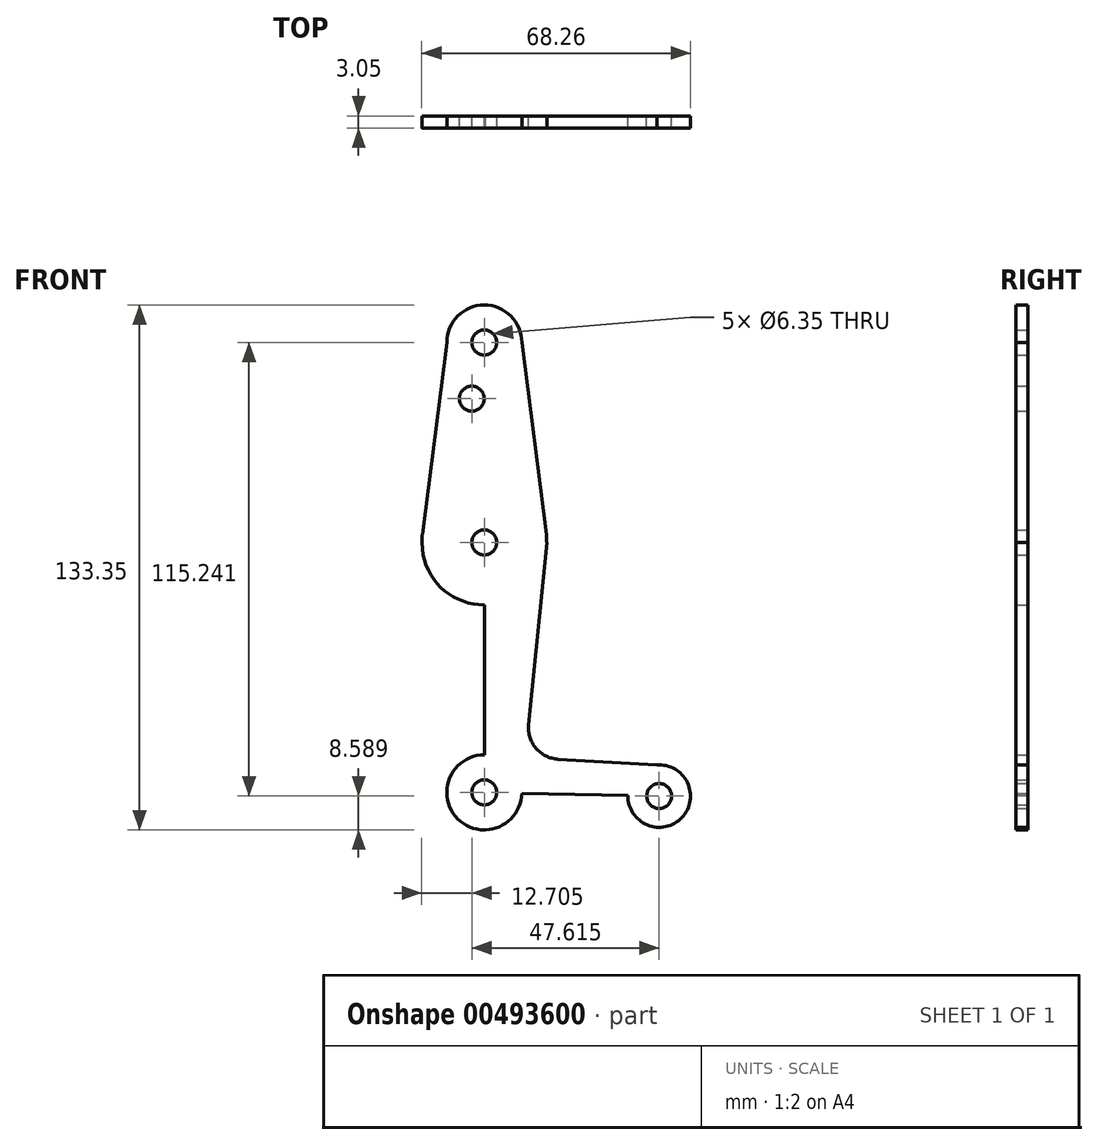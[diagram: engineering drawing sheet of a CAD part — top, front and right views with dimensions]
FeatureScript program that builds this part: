
annotation { "Feature Type Name" : "Feature", "Feature Type Description" : "" }
export const myFeature = defineFeature(function(context is Context, id is Id, definition is map)
    precondition{}
    {
        {
            var Q0;
            Q0=qCreatedBy(makeId("Front.planeOp"),FACE);
            var sketch = newSketch(context, id + "F0", { "sketchPlane" : qUnion([Q0])});
            skCircle(sketch, "E0", {"center": v(0, 0) * mm, "radius": 15.88 * mm});
            skLineSegment(sketch, "E1", {"start": v(0, 0) * mm, "end": v(0, -63.5) * mm});
            skCircle(sketch, "E2", {"center": v(0, -63.5) * mm, "radius": 3.18 * mm});
            skCircle(sketch, "E3", {"center": v(0, -63.5) * mm, "radius": 9.53 * mm});
            skLineSegment(sketch, "E4", {"start": v(-15.88, 0) * mm, "end": v(-9.48, -64.44) * mm});
            skLineSegment(sketch, "E5", {"start": v(15.88, 0) * mm, "end": v(11.27, -46.34) * mm});
            skCircle(sketch, "E6", {"center": v(-3.18, 36.53) * mm, "radius": 3.18 * mm});
            skCircle(sketch, "E7", {"center": v(0, 50.8) * mm, "radius": 9.53 * mm});
            skCircle(sketch, "E8", {"center": v(0, 50.8) * mm, "radius": 3.18 * mm});
            skLineSegment(sketch, "E9", {"start": v(9.52, 50.8) * mm, "end": v(15.88, 1) * mm});
            skLineSegment(sketch, "E10", {"start": v(-9.52, 50.8) * mm, "end": v(-15.88, 1) * mm});
            skLineSegment(sketch, "E11", {"start": v(0, -63.5) * mm, "end": v(44.44, -64.44) * mm});
            skCircle(sketch, "E12", {"center": v(44.44, -64.44) * mm, "radius": 7.94 * mm});
            skLineSegment(sketch, "E13", {"start": v(0, -73.03) * mm, "end": v(44.56, -72.38) * mm});
            skLineSegment(sketch, "E14", {"start": v(43.82, -56.53) * mm, "end": v(18.72, -55.07) * mm});
            skPoint(sketch, "E15.newPointA", {"position": v(9.57, -63.5) * mm});
            skArc(sketch, "E15.filletArc", {"start": v(11.27, -46.34) * mm, "mid": v(13.14, -52.3) * mm, "end": v(18.72, -55.07) * mm});
            skCircle(sketch, "E16", {"center": v(0, 0) * mm, "radius": 3.18 * mm});
            skCircle(sketch, "E17", {"center": v(44.44, -64.44) * mm, "radius": 3.18 * mm});
            skSolve(sketch);
        }
        {
            var Q0;
            Q0=makeQuery(id+"F0.imprint","IMPRINT",FACE,{"disambiguationData":[TD([[makeQuery(id+"F0.imprint","IMPRINT",EDGE,{"derivedFrom":sQuery(id+"F0.wireOp",EDGE,"E6")}),-1.0]])]});
            var Q1;
            Q1=makeQuery(id+"F0.imprint","IMPRINT",FACE,{"disambiguationData":[TD([[makeQuery(id+"F0.imprint","IMPRINT",EDGE,{"derivedFrom":sQuery(id+"F0.wireOp",EDGE,"E16")}),-1.0]])]});
            var Q2;
            {var subQ0=sQuery(id+"F0.wireOp",EDGE,"E4");var subQ1=sQuery(id+"F0.wireOp",EDGE,"E0");var subQ2=makeQuery(id+"F0.imprint","INTERSECT",VERTEX,{"disambiguationData":[OD(1.0)],"derivedFrom":[subQ1,subQ0]});Q2=makeQuery(id+"F0.imprint","IMPRINT",FACE,{"disambiguationData":[TD([[makeQuery(id+"F0.imprint","IMPRINT",EDGE,{"disambiguationData":[TD([[subQ2,-1.0]])],"derivedFrom":subQ1}),-1.0]])]});}
            var Q3;
            {var subQ12=sQuery(id+"F0.wireOp",EDGE,"E14");Q3=makeQuery(id+"F0.imprint","IMPRINT",FACE,{"disambiguationData":[TD([[makeQuery(id+"F0.imprint","IMPRINT",EDGE,{"derivedFrom":subQ12}),1.0]])]});}
            var Q4;
            {var subQ0=sQuery(id+"F0.wireOp",EDGE,"E13");var subQ1=sQuery(id+"F0.wireOp",EDGE,"E3");var subQ2=makeQuery(id+"F0.imprint","INTERSECT",VERTEX,{"disambiguationData":[OD(1.0)],"derivedFrom":[subQ1,subQ0]});Q4=makeQuery(id+"F0.imprint","IMPRINT",FACE,{"disambiguationData":[TD([[makeQuery(id+"F0.imprint","IMPRINT",EDGE,{"disambiguationData":[TD([[subQ2,-1.0]])],"derivedFrom":subQ1}),-1.0]])]});}
            var Q5;
            {var subQ0=sQuery(id+"F0.wireOp",EDGE,"E3");var subQ2=sQuery(id+"F0.wireOp",EDGE,"E1");var subQ3=makeQuery(id+"F0.imprint","INTERSECT",VERTEX,{"derivedFrom":[subQ2,subQ0]});Q5=makeQuery(id+"F0.imprint","IMPRINT",FACE,{"disambiguationData":[TD([[makeQuery(id+"F0.imprint","IMPRINT",EDGE,{"disambiguationData":[TD([[subQ3,-1.0]])],"derivedFrom":subQ2}),-1.0]])]});}
            var Q6;
            {var subQ0=sQuery(id+"F0.wireOp",EDGE,"E3");var subQ1=sQuery(id+"F0.wireOp",EDGE,"E1");var subQ2=makeQuery(id+"F0.imprint","INTERSECT",VERTEX,{"derivedFrom":[subQ1,subQ0]});Q6=makeQuery(id+"F0.imprint","IMPRINT",FACE,{"disambiguationData":[TD([[makeQuery(id+"F0.imprint","IMPRINT",EDGE,{"disambiguationData":[TD([[subQ2,-1.0]])],"derivedFrom":subQ1}),1.0]])]});}
            var Q7;
            Q7=makeQuery(id+"F0.imprint","IMPRINT",FACE,{"disambiguationData":[TD([[makeQuery(id+"F0.imprint","IMPRINT",EDGE,{"derivedFrom":sQuery(id+"F0.wireOp",EDGE,"E17")}),-1.0]])]});
            var Q8;
            Q8=makeQuery(id+"F0.imprint","IMPRINT",FACE,{"disambiguationData":[TD([[makeQuery(id+"F0.imprint","IMPRINT",EDGE,{"derivedFrom":sQuery(id+"F0.wireOp",EDGE,"E8")}),-1.0]])]});
            extrude(context, id + "F1", {"entities" : qUnion([Q0, Q1, Q2, Q3, Q4, Q5, Q6, Q7, Q8]), "depth" : 3.05 * mm});
        }
    });
